# Revit family: BC_Hitachi_RAS-4-6H(V)NC1E_LOD400
name_source: partatom
category: Equipement de génie climatique
revit_build: Autodesk Revit 2017 (Build: 20160225_1515(x64)
units: mm (PartAtom-declared; Revit-internal decimal feet)

## family parameters
Basée sur le plan de construction = Non
Cote de connecteur circulaire = Utiliser le diamètre
Couper avec des vides une fois chargée = Non
Numéro OmniClass = 23.75.00.00
Partagée = Non
Point de calcul de pièce = Non
Titre OmniClass = Climate Control (HVAC)
Toujours verticalement = Oui
Type d'élément = Normal

## types (6) — shared parameters
BC_MODEL_ID = 166715
BC_OBJECT_ID = 29484
BC_OBJECT_VERSION = #4
Compressor Type = Scroll DC Inverter driven
Frequency = 50 Hz
Gas Diameter = 15.88 mm
Heating Capacity Min = 5 kW
Height difference between OU & IU (higher OU) = 30000.00 mm
Height difference between OU & IU (lower OU) = 20000.00 mm
Liquid Diameter = 9.52 mm
Manufacturer = Hitachi Air Conditioning Europe SAS
Material = IVX Material
Maximum chargless piping length = 30000.00 mm
Maximum connectable indoor units = 4
Maximum connected capacity = 115 %
Miminum piping length = 5000.00 mm
Minimum connectable indoor units = 1
Minimum connected capacity = 90 %
Modèle = RAS-4-6H(V)NC1E
Name BIM&CO = Outdoor Unit
Overall Depth = 370.00 mm
Overall Height = 1140.00 mm
Overall Width = 950.00 mm
Refrigerant Type = R410A
Refrigerant charge before shipment = 3.20 kg
Size of transmission cable between indoor unit and outdoor unit = 2 x 0.75 mm²
Starting current (A) = Less than maximum current
Wired Remote control model (Optional) = PC-ARFPE

## per-type parameters (varying)
| type | BC_VARIANT_ID | Coefficient of Performance (COP) | Cooling Capacity | Cooling Capacity Max | Cooling Capacity Min | Cooling Running Current | Cooling Sound Pressure Level | Energy efficiency ratio (EER) | Heating Capacity | Heating Capacity Max | Heating Running Current | Heating Sound Pressure Level | Maximum Current | Maximum piping length (additional refrigerant needed) | Net Weight | Nominal Air Flow | Nominal Voltage | Number of Poles | Recommended circuit breaker | Size of power cable (according to EN 60335-1) | Sound level | Sound pressure level Night mode cooling (dB(A)) |
| RAS-4HVNC1E | 192745 | 4.57 | 10 kW | 11 kW | 5 kW | 11 A | 52 | 3.7 | 11 kW | 14 kW | 10 A | 54 | 29 A | 70 m (40 g/m) | 79.00 kg | 3720.0 m³/h | 230 V | 1 | 32 A | 3 x 6.0 mm² | 68 | 50 |
| RAS-5HVNC1E | 192753 | 3.89 | 13 kW | 14 kW | 6 kW | 16 A | 52 | 3.37 | 14 kW | 18 kW | 15 A | 54 | 29 A | 75 m (60 g/m) | 89.00 kg | 4080.0 m³/h | 230 V | 1 | 32 A | 3 x 6.0 mm² | 69 | 50 |
| RAS-6HVNC1E | 192760 | 3.56 | 14 kW | 16 kW | 6 kW | 18 A | 55 | 3.26 | 16 kW | 20 kW | 19 A | 57 | 29 A | 75 m (60 g/m) | 89.00 kg | 4800.0 m³/h | 230 V | 1 | 32 A | 3 x 6.0 mm² | 71 | 53 |
| RAS-4HNC1E | 192771 | 4.57 | 10 kW | 11 kW | 5 kW | 4 A | 52 | 3.7 | 11 kW | 14 kW | 4 A | 54 | 16 A | 70 m (40 g/m) | 79.00 kg | 4500.0 m³/h | 400 V | 3 | 20 A | 5 x 4.0 mm² | 68 | 50 |
| RAS-5HNC1E | 192770 | 3.89 | 13 kW | 14 kW | 6 kW | 6 A | 52 | 3.37 | 14 kW | 18 kW | 6 A | 54 | 16 A | 75 m (60 g/m) | 89.00 kg | 4500.0 m³/h | 400 V | 3 | 20 A | 5 x 4.0 mm² | 69 | 50 |
| RAS-6HNC1E | 192772 | 3.56 | 14 kW | 16 kW | 6 kW | 7 A | 55 | 3.26 | 16 kW | 20 kW | 7 A | 57 | 16 A | 75 m (60 g/m) | 89.00 kg | 4800.0 m³/h | 400 V | 3 | 20 A | 5 x 4.0 mm² | 71 | 53 |

note: column(s) folded — value = type name in every type: Commentaires du type, Reference

## geometry (parser evidence)
native form markers: Blend x2
no freeform markers — native parametric forms only
